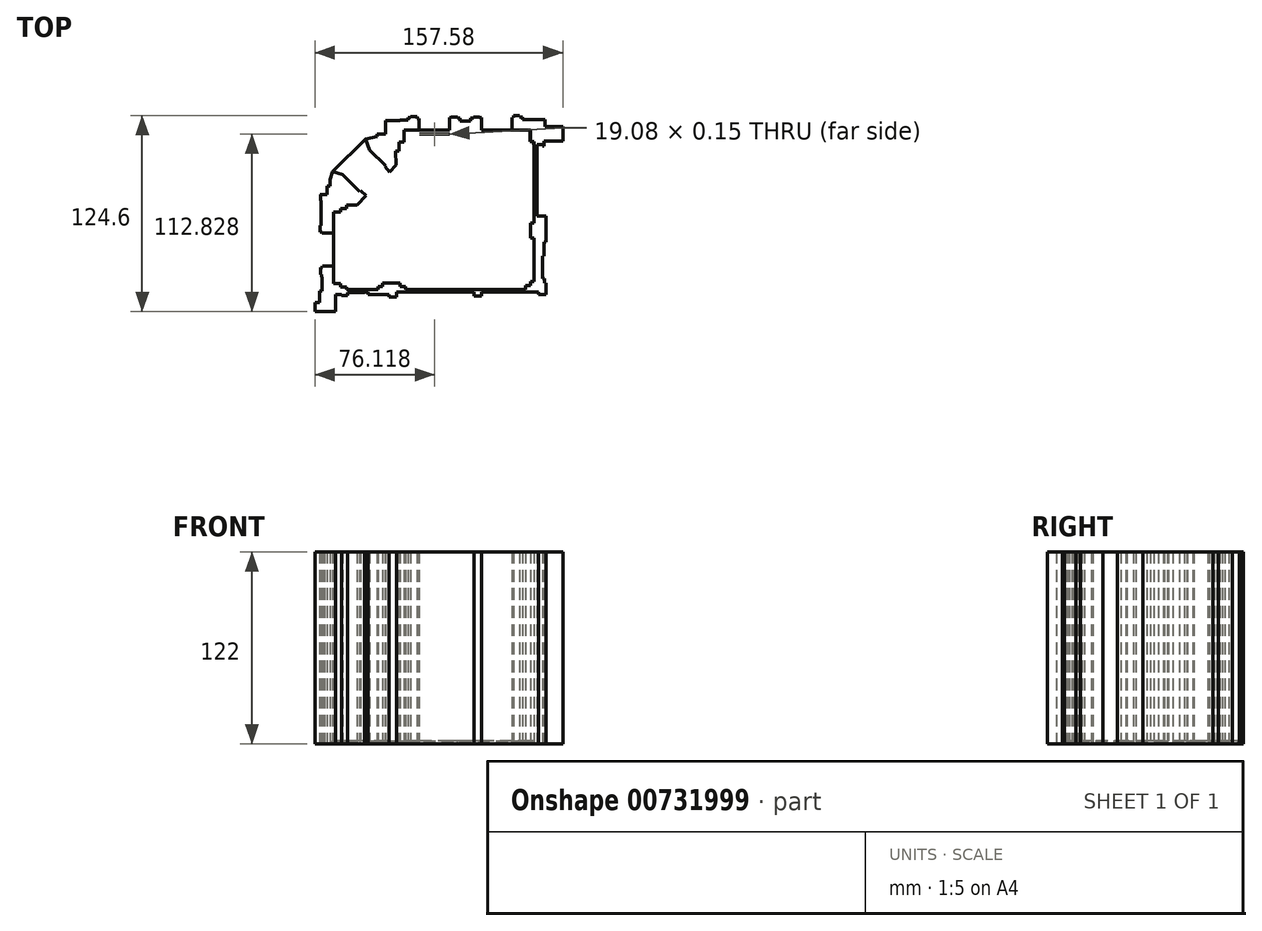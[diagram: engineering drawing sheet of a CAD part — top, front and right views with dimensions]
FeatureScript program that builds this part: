
annotation { "Feature Type Name" : "Feature", "Feature Type Description" : "" }
export const myFeature = defineFeature(function(context is Context, id is Id, definition is map)
    precondition{}
    {
        {
            var Q0;
            Q0=qCreatedBy(makeId("Top.planeOp"),FACE);
            var sketch = newSketch(context, id + "F0", { "sketchPlane" : qUnion([Q0])});
            skLineSegment(sketch, "E0", {"start": v(100, 30.78) * mm, "end": v(19.62, 30.78) * mm});
            skLineSegment(sketch, "E1", {"start": v(14.37, 17.38) * mm, "end": v(14.67, 8.47) * mm});
            skLineSegment(sketch, "E2", {"start": v(10.68, 4.23) * mm, "end": v(7.6, 7.76) * mm});
            skLineSegment(sketch, "E3", {"start": v(-10.22, -16.86) * mm, "end": v(-16.88, -16.86) * mm});
            skLineSegment(sketch, "E4", {"start": v(-16.88, -16.86) * mm, "end": v(-16.88, -19.03) * mm});
            skLineSegment(sketch, "E5", {"start": v(-16.88, -19.03) * mm, "end": v(-20.5, -19.03) * mm});
            skLineSegment(sketch, "E6", {"start": v(-20.5, -19.03) * mm, "end": v(-20.5, -21.2) * mm});
            skLineSegment(sketch, "E7", {"start": v(-20.5, -21.2) * mm, "end": v(-24.94, -21.2) * mm});
            skLineSegment(sketch, "E8", {"start": v(-24.94, -21.2) * mm, "end": v(-24.94, -66.6) * mm});
            skLineSegment(sketch, "E9", {"start": v(-24.94, -66.6) * mm, "end": v(-20.5, -66.6) * mm});
            skLineSegment(sketch, "E10", {"start": v(-20.5, -66.6) * mm, "end": v(-20.5, -68.85) * mm});
            skLineSegment(sketch, "E11", {"start": v(-20.5, -68.85) * mm, "end": v(-16.88, -68.85) * mm});
            skLineSegment(sketch, "E12", {"start": v(-16.88, -68.85) * mm, "end": v(-16.88, -70.47) * mm});
            skLineSegment(sketch, "E13", {"start": v(-16.88, -70.47) * mm, "end": v(3.12, -70.47) * mm});
            skLineSegment(sketch, "E14", {"start": v(3.12, -70.47) * mm, "end": v(3.12, -68.58) * mm});
            skLineSegment(sketch, "E15", {"start": v(3.12, -68.58) * mm, "end": v(6.2, -68.58) * mm});
            skLineSegment(sketch, "E16", {"start": v(6.2, -68.58) * mm, "end": v(6.2, -66.38) * mm});
            skLineSegment(sketch, "E17", {"start": v(6.2, -66.38) * mm, "end": v(17.27, -66.38) * mm});
            skLineSegment(sketch, "E18", {"start": v(17.27, -66.38) * mm, "end": v(17.27, -68.45) * mm});
            skLineSegment(sketch, "E19", {"start": v(17.27, -68.45) * mm, "end": v(20.68, -68.45) * mm});
            skLineSegment(sketch, "E20", {"start": v(20.68, -68.45) * mm, "end": v(20.68, -70.43) * mm});
            skLineSegment(sketch, "E21", {"start": v(20.68, -70.43) * mm, "end": v(96.86, -70.43) * mm});
            skLineSegment(sketch, "E22", {"start": v(96.86, -70.43) * mm, "end": v(96.86, -67.86) * mm});
            skLineSegment(sketch, "E23", {"start": v(96.86, -67.86) * mm, "end": v(100.14, -67.86) * mm});
            skLineSegment(sketch, "E24", {"start": v(100.14, -67.86) * mm, "end": v(100.14, -65.47) * mm});
            skLineSegment(sketch, "E25", {"start": v(100.14, -65.47) * mm, "end": v(102.3, -65.47) * mm});
            skLineSegment(sketch, "E26", {"start": v(102.3, -65.47) * mm, "end": v(102.3, -37.74) * mm});
            skLineSegment(sketch, "E27", {"start": v(102.3, -37.74) * mm, "end": v(100, -37.74) * mm});
            skLineSegment(sketch, "E28", {"start": v(100, -37.74) * mm, "end": v(100, -28.3) * mm});
            skLineSegment(sketch, "E29", {"start": v(100, -28.3) * mm, "end": v(102.15, -28.3) * mm});
            skLineSegment(sketch, "E30", {"start": v(102.15, -28.3) * mm, "end": v(102.15, 23.5) * mm});
            skLineSegment(sketch, "E31", {"start": v(102.15, 23.5) * mm, "end": v(100, 23.5) * mm});
            skLineSegment(sketch, "E32", {"start": v(100, 23.5) * mm, "end": v(100, 30.78) * mm});
            skLineSegment(sketch, "E33", {"start": v(102.15, -23.98) * mm, "end": v(109.78, -23.98) * mm});
            skLineSegment(sketch, "E34", {"start": v(109.78, -23.98) * mm, "end": v(109.78, -40.2) * mm});
            skLineSegment(sketch, "E35", {"start": v(109.78, -40.2) * mm, "end": v(108.53, -40.2) * mm});
            skLineSegment(sketch, "E36", {"start": v(108.53, -40.2) * mm, "end": v(108.53, -49.32) * mm});
            skLineSegment(sketch, "E37", {"start": v(108.53, -49.32) * mm, "end": v(107.6, -49.32) * mm});
            skLineSegment(sketch, "E38", {"start": v(107.6, -49.32) * mm, "end": v(107.6, -63.66) * mm});
            skLineSegment(sketch, "E39", {"start": v(107.6, -63.66) * mm, "end": v(108.9, -63.66) * mm});
            skLineSegment(sketch, "E40", {"start": v(108.9, -63.66) * mm, "end": v(108.9, -66.41) * mm});
            skLineSegment(sketch, "E41", {"start": v(108.9, -66.41) * mm, "end": v(109.78, -66.41) * mm});
            skLineSegment(sketch, "E42", {"start": v(109.78, -66.41) * mm, "end": v(109.78, -73.81) * mm});
            skLineSegment(sketch, "E43", {"start": v(109.78, -73.81) * mm, "end": v(105, -73.81) * mm});
            skLineSegment(sketch, "E44", {"start": v(105, -73.81) * mm, "end": v(105, -72.02) * mm});
            skLineSegment(sketch, "E45", {"start": v(105, -72.02) * mm, "end": v(68.84, -72.02) * mm});
            skLineSegment(sketch, "E46", {"start": v(68.84, -72.02) * mm, "end": v(68.84, -74.47) * mm});
            skLineSegment(sketch, "E47", {"start": v(68.84, -74.47) * mm, "end": v(64.15, -74.47) * mm});
            skLineSegment(sketch, "E48", {"start": v(64.15, -74.47) * mm, "end": v(64.15, -72.02) * mm});
            skLineSegment(sketch, "E49", {"start": v(64.15, -72.02) * mm, "end": v(15, -72.02) * mm});
            skLineSegment(sketch, "E50", {"start": v(15, -72.02) * mm, "end": v(15, -75.12) * mm});
            skLineSegment(sketch, "E51", {"start": v(15, -75.12) * mm, "end": v(10.3, -75.12) * mm});
            skLineSegment(sketch, "E52", {"start": v(10.3, -75.12) * mm, "end": v(10.3, -73.52) * mm});
            skLineSegment(sketch, "E53", {"start": v(10.3, -73.52) * mm, "end": v(-3.14, -73.52) * mm});
            skLineSegment(sketch, "E54", {"start": v(-3.14, -73.52) * mm, "end": v(-3.14, -72.02) * mm});
            skLineSegment(sketch, "E55", {"start": v(-3.14, -72.02) * mm, "end": v(-5.41, -72.02) * mm});
            skLineSegment(sketch, "E56", {"start": v(-16.3, -72.35) * mm, "end": v(-16.3, -74.28) * mm});
            skLineSegment(sketch, "E57", {"start": v(-16.3, -74.28) * mm, "end": v(-19.89, -74.28) * mm});
            skLineSegment(sketch, "E58", {"start": v(-19.89, -74.28) * mm, "end": v(-19.89, -73.55) * mm});
            skLineSegment(sketch, "E59", {"start": v(-19.89, -73.55) * mm, "end": v(-23.83, -73.55) * mm});
            skLineSegment(sketch, "E60", {"start": v(-23.83, -73.55) * mm, "end": v(-23.83, -84.62) * mm});
            skLineSegment(sketch, "E61", {"start": v(-23.83, -84.62) * mm, "end": v(-36.93, -84.62) * mm});
            skLineSegment(sketch, "E62", {"start": v(-36.93, -84.62) * mm, "end": v(-36.93, -78.83) * mm});
            skLineSegment(sketch, "E63", {"start": v(-36.93, -78.83) * mm, "end": v(-33.87, -78.83) * mm});
            skLineSegment(sketch, "E64", {"start": v(-33.87, -78.83) * mm, "end": v(-33.87, -71.33) * mm});
            skLineSegment(sketch, "E65", {"start": v(-33.87, -71.33) * mm, "end": v(-32.2, -71.33) * mm});
            skLineSegment(sketch, "E66", {"start": v(-32.2, -71.33) * mm, "end": v(-32.2, -62.56) * mm});
            skLineSegment(sketch, "E67", {"start": v(-32.2, -62.56) * mm, "end": v(-32.7, -62.56) * mm});
            skLineSegment(sketch, "E68", {"start": v(-32.7, -62.56) * mm, "end": v(-32.7, -60.9) * mm});
            skLineSegment(sketch, "E69", {"start": v(-32.7, -60.9) * mm, "end": v(-33.3, -60.9) * mm});
            skLineSegment(sketch, "E70", {"start": v(-33.3, -60.9) * mm, "end": v(-33.3, -56.5) * mm});
            skLineSegment(sketch, "E71", {"start": v(-33.3, -56.5) * mm, "end": v(-32.1, -56.5) * mm});
            skLineSegment(sketch, "E72", {"start": v(-32.1, -56.5) * mm, "end": v(-32.1, -55.62) * mm});
            skLineSegment(sketch, "E73", {"start": v(-32.1, -55.62) * mm, "end": v(-24.94, -55.62) * mm});
            skLineSegment(sketch, "E74.top", {"start": v(-16.3, -72.35) * mm, "end": v(-5.41, -72.35) * mm});
            skLineSegment(sketch, "E74.right", {"start": v(-5.41, -72.02) * mm, "end": v(-5.41, -72.35) * mm});
            skLineSegment(sketch, "E75", {"start": v(104.08, -23.98) * mm, "end": v(104.08, 21.47) * mm});
            skLineSegment(sketch, "E76.bottom", {"start": v(88.6, 28.28) * mm, "end": v(68.96, 28.28) * mm});
            skLineSegment(sketch, "E76.top", {"start": v(88.6, 17.82) * mm, "end": v(68.96, 17.82) * mm});
            skLineSegment(sketch, "E76.left", {"start": v(88.6, 28.28) * mm, "end": v(88.6, 17.82) * mm});
            skLineSegment(sketch, "E76.right", {"start": v(68.96, 28.28) * mm, "end": v(68.96, 17.82) * mm});
            skLineSegment(sketch, "E77.bottom", {"start": v(48.73, 28.28) * mm, "end": v(29.65, 28.28) * mm});
            skLineSegment(sketch, "E77.top", {"start": v(48.73, 17.82) * mm, "end": v(29.65, 17.82) * mm});
            skLineSegment(sketch, "E77.left", {"start": v(48.73, 28.28) * mm, "end": v(48.73, 17.82) * mm});
            skLineSegment(sketch, "E77.right", {"start": v(29.65, 28.28) * mm, "end": v(29.65, 17.82) * mm});
            skLineSegment(sketch, "E78", {"start": v(14.37, 17.38) * mm, "end": v(16.66, 17.38) * mm});
            skLineSegment(sketch, "E79", {"start": v(16.66, 17.38) * mm, "end": v(16.66, 23.03) * mm});
            skLineSegment(sketch, "E80", {"start": v(16.66, 23.03) * mm, "end": v(19.9, 23.03) * mm});
            skLineSegment(sketch, "E81", {"start": v(19.9, 23.03) * mm, "end": v(19.9, 30.78) * mm});
            skLineSegment(sketch, "E82", {"start": v(19.9, 30.78) * mm, "end": v(29.26, 30.78) * mm});
            skLineSegment(sketch, "E83", {"start": v(29.26, 30.78) * mm, "end": v(29.26, 38.23) * mm});
            skLineSegment(sketch, "E84", {"start": v(29.26, 38.23) * mm, "end": v(28.12, 38.23) * mm});
            skLineSegment(sketch, "E85", {"start": v(28.12, 38.23) * mm, "end": v(28.12, 39.27) * mm});
            skLineSegment(sketch, "E86", {"start": v(28.12, 39.27) * mm, "end": v(23.9, 39.27) * mm});
            skLineSegment(sketch, "E87", {"start": v(23.9, 39.27) * mm, "end": v(23.9, 38.64) * mm});
            skLineSegment(sketch, "E88", {"start": v(23.9, 38.64) * mm, "end": v(22.3, 38.64) * mm});
            skLineSegment(sketch, "E89", {"start": v(22.3, 38.64) * mm, "end": v(22.3, 37.04) * mm});
            skLineSegment(sketch, "E90", {"start": v(22.3, 37.04) * mm, "end": v(17.2, 37.04) * mm});
            skLineSegment(sketch, "E91", {"start": v(17.2, 37.04) * mm, "end": v(17.2, 36.7) * mm});
            skLineSegment(sketch, "E92", {"start": v(17.2, 36.7) * mm, "end": v(7.86, 36.7) * mm});
            skLineSegment(sketch, "E93", {"start": v(7.86, 36.7) * mm, "end": v(8.12, 28.3) * mm});
            skLineSegment(sketch, "E94", {"start": v(8.12, 28.3) * mm, "end": v(2.65, 28.3) * mm});
            skLineSegment(sketch, "E95", {"start": v(2.65, 28.3) * mm, "end": v(2.65, 26.75) * mm});
            skLineSegment(sketch, "E96", {"start": v(2.65, 26.75) * mm, "end": v(-4.82, 25.12) * mm});
            skLineSegment(sketch, "E97", {"start": v(-4.82, 25.12) * mm, "end": v(-2.29, 18.24) * mm});
            skLineSegment(sketch, "E98", {"start": v(8.12, 8.35) * mm, "end": v(-2.29, 18.24) * mm});
            skLineSegment(sketch, "E99", {"start": v(8.12, 8.35) * mm, "end": v(7.6, 7.76) * mm});
            skLineSegment(sketch, "E100", {"start": v(-4.42, -10.92) * mm, "end": v(-10.22, -16.86) * mm});
            skLineSegment(sketch, "E101", {"start": v(-24.94, -34.61) * mm, "end": v(-32.4, -34.61) * mm});
            skLineSegment(sketch, "E102", {"start": v(-33.67, -33.94) * mm, "end": v(-33.67, -29.77) * mm});
            skLineSegment(sketch, "E103", {"start": v(-33.67, -29.77) * mm, "end": v(-33.03, -29.77) * mm});
            skLineSegment(sketch, "E104", {"start": v(-33.03, -29.77) * mm, "end": v(-33.03, -13.85) * mm});
            skLineSegment(sketch, "E105", {"start": v(-33.03, -13.85) * mm, "end": v(-33.37, -13.85) * mm});
            skLineSegment(sketch, "E106", {"start": v(-33.37, -13.85) * mm, "end": v(-33.37, -10.27) * mm});
            skLineSegment(sketch, "E107", {"start": v(-33.67, -10.27) * mm, "end": v(-33.37, -10.27) * mm});
            skLineSegment(sketch, "E108", {"start": v(-33.67, -10.27) * mm, "end": v(-33.67, -10.09) * mm});
            skLineSegment(sketch, "E109", {"start": v(-33.67, -10.09) * mm, "end": v(-30.72, -10.09) * mm});
            skLineSegment(sketch, "E110", {"start": v(-29.22, -10.27) * mm, "end": v(-29.22, -4.8) * mm});
            skLineSegment(sketch, "E111", {"start": v(-29.22, -4.8) * mm, "end": v(-27.15, -4.8) * mm});
            skLineSegment(sketch, "E112", {"start": v(-27.15, -4.8) * mm, "end": v(-27.15, -0.77) * mm});
            skLineSegment(sketch, "E113", {"start": v(-27.15, -0.77) * mm, "end": v(-25.68, 4.32) * mm});
            skLineSegment(sketch, "E114", {"start": v(-25.68, 4.32) * mm, "end": v(-19.3, 2.48) * mm});
            skLineSegment(sketch, "E115", {"start": v(-19.3, 2.48) * mm, "end": v(-8.62, -8.4) * mm});
            skLineSegment(sketch, "E116", {"start": v(-8.62, -8.4) * mm, "end": v(-7.74, -7.67) * mm});
            skLineSegment(sketch, "E117", {"start": v(-30.72, -10.09) * mm, "end": v(-30.72, -10.27) * mm});
            skLineSegment(sketch, "E118", {"start": v(-30.72, -10.27) * mm, "end": v(-29.22, -10.27) * mm});
            skLineSegment(sketch, "E119", {"start": v(-4.42, -10.92) * mm, "end": v(-7.74, -7.67) * mm});
            skLineSegment(sketch, "E120", {"start": v(-32.4, -34.61) * mm, "end": v(-32.4, -33.94) * mm});
            skLineSegment(sketch, "E121", {"start": v(-32.4, -33.94) * mm, "end": v(-33.67, -33.94) * mm});
            skPoint(sketch, "E122.orphan", {"position": v(-33.67, -34.61) * mm});
            skLineSegment(sketch, "E123", {"start": v(48.76, 30.78) * mm, "end": v(69.02, 30.78) * mm});
            skLineSegment(sketch, "E124", {"start": v(69.02, 30.78) * mm, "end": v(69.02, 38.67) * mm});
            skLineSegment(sketch, "E125", {"start": v(69.02, 38.67) * mm, "end": v(67.73, 38.67) * mm});
            skLineSegment(sketch, "E126", {"start": v(67.73, 38.67) * mm, "end": v(67.73, 39) * mm});
            skLineSegment(sketch, "E127", {"start": v(67.73, 39) * mm, "end": v(63.74, 39) * mm});
            skLineSegment(sketch, "E128", {"start": v(63.74, 39) * mm, "end": v(63.74, 38.36) * mm});
            skLineSegment(sketch, "E129", {"start": v(63.74, 38.36) * mm, "end": v(62.08, 38.36) * mm});
            skLineSegment(sketch, "E130", {"start": v(62.08, 38.36) * mm, "end": v(62.08, 36.47) * mm});
            skLineSegment(sketch, "E131", {"start": v(62.08, 36.47) * mm, "end": v(55.28, 36.47) * mm});
            skLineSegment(sketch, "E132", {"start": v(55.28, 36.47) * mm, "end": v(55.28, 38.36) * mm});
            skLineSegment(sketch, "E133", {"start": v(55.28, 38.36) * mm, "end": v(53.72, 38.36) * mm});
            skLineSegment(sketch, "E134", {"start": v(53.72, 38.36) * mm, "end": v(53.72, 39) * mm});
            skLineSegment(sketch, "E135", {"start": v(53.72, 39) * mm, "end": v(49.68, 39) * mm});
            skLineSegment(sketch, "E136", {"start": v(49.68, 39) * mm, "end": v(49.68, 38.67) * mm});
            skLineSegment(sketch, "E137", {"start": v(49.68, 38.67) * mm, "end": v(48.76, 38.67) * mm});
            skLineSegment(sketch, "E138", {"start": v(48.76, 38.67) * mm, "end": v(48.76, 30.78) * mm});
            skLineSegment(sketch, "E139", {"start": v(99.67, 30.78) * mm, "end": v(99.67, 23.5) * mm});
            skLineSegment(sketch, "E140", {"start": v(99.67, 23.5) * mm, "end": v(102.12, 23.5) * mm});
            skLineSegment(sketch, "E141", {"start": v(102.12, 23.5) * mm, "end": v(102.12, 21.47) * mm});
            skLineSegment(sketch, "E142", {"start": v(102.12, 21.47) * mm, "end": v(107.62, 21.47) * mm});
            skLineSegment(sketch, "E143", {"start": v(107.62, 21.47) * mm, "end": v(107.62, 20.5) * mm});
            skLineSegment(sketch, "E144", {"start": v(107.62, 20.5) * mm, "end": v(108.74, 20.5) * mm});
            skLineSegment(sketch, "E145", {"start": v(108.74, 20.5) * mm, "end": v(108.74, 23.95) * mm});
            skLineSegment(sketch, "E146", {"start": v(108.74, 23.95) * mm, "end": v(120.65, 23.95) * mm});
            skLineSegment(sketch, "E147", {"start": v(120.65, 23.95) * mm, "end": v(120.65, 32.97) * mm});
            skLineSegment(sketch, "E148", {"start": v(120.65, 32.97) * mm, "end": v(109.3, 32.97) * mm});
            skLineSegment(sketch, "E149", {"start": v(109.3, 32.97) * mm, "end": v(109.3, 37.43) * mm});
            skLineSegment(sketch, "E150", {"start": v(109.3, 37.43) * mm, "end": v(94.85, 37.43) * mm});
            skLineSegment(sketch, "E151", {"start": v(94.85, 37.43) * mm, "end": v(94.85, 39.05) * mm});
            skLineSegment(sketch, "E152", {"start": v(94.85, 39.05) * mm, "end": v(93.23, 39.05) * mm});
            skLineSegment(sketch, "E153", {"start": v(93.23, 39.05) * mm, "end": v(93.23, 39.98) * mm});
            skLineSegment(sketch, "E154", {"start": v(93.23, 39.98) * mm, "end": v(89.15, 39.98) * mm});
            skLineSegment(sketch, "E155", {"start": v(89.15, 39.98) * mm, "end": v(89.15, 38.67) * mm});
            skLineSegment(sketch, "E156", {"start": v(89.15, 38.67) * mm, "end": v(88.27, 38.67) * mm});
            skLineSegment(sketch, "E157", {"start": v(88.27, 38.67) * mm, "end": v(88.27, 30.78) * mm});
            skLineSegment(sketch, "E158", {"start": v(88.27, 30.78) * mm, "end": v(99.67, 30.78) * mm});
            skLineSegment(sketch, "E159.bottom", {"start": v(48.76, 28.13) * mm, "end": v(29.26, 28.13) * mm});
            skLineSegment(sketch, "E159.left", {"start": v(48.76, 28.13) * mm, "end": v(48.76, 18.13) * mm});
            skLineSegment(sketch, "E159.right", {"start": v(29.26, 28.13) * mm, "end": v(29.26, 18.13) * mm});
            skLineSegment(sketch, "E160.bottom", {"start": v(-22.44, -34.61) * mm, "end": v(-12.44, -34.61) * mm});
            skLineSegment(sketch, "E160.top", {"start": v(-22.44, -55.62) * mm, "end": v(-12.44, -55.62) * mm});
            skLineSegment(sketch, "E160.left", {"start": v(-22.44, -34.61) * mm, "end": v(-22.44, -55.62) * mm});
            skLineSegment(sketch, "E160.right", {"start": v(-12.44, -34.61) * mm, "end": v(-12.44, -55.62) * mm});
            skLineSegment(sketch, "E161", {"start": v(10.68, 4.23) * mm, "end": v(14.67, 8.47) * mm});
            skLineSegment(sketch, "E162", {"start": v(10.68, 4.23) * mm, "end": v(-4.42, -10.92) * mm});
            skFitSpline(sketch, "E163", {"points": [v(102.15, 8.94) * mm, v(78.29, 3.93) * mm, v(66.58, -13.62) * mm, v(53.72, -35.8) * mm, v(24.2, -40.24) * mm, v(1.71, -50.69) * mm, v(-5.41, -70.47) * mm], "startDerivative": vector(-103.23, 11.75) * mm, "endDerivative": vector(-2.21, -218.2) * mm});
            skLineSegment(sketch, "E164", {"start": v(102.15, -15.64) * mm, "end": v(55.24, -70.43) * mm, "construction": true});
            skArc(sketch, "E165", {"start": v(100, -28.3) * mm, "mid": v(70.38, -40.66) * mm, "end": v(58.36, -70.43) * mm});
            skLineSegment(sketch, "E166", {"start": v(100, -28.3) * mm, "end": v(75.52, -28.3) * mm, "construction": true});
            skLineSegment(sketch, "E167", {"start": v(-4.82, 25.12) * mm, "end": v(-25.68, 4.32) * mm});
            skSolve(sketch);
        }
        {
            var Q0;
            {var subQ6=sQuery(id+"F0.wireOp",EDGE,"E9");Q0=makeQuery(id+"F0.imprint","IMPRINT",FACE,{"disambiguationData":[TD([[makeQuery(id+"F0.imprint","IMPRINT",EDGE,{"derivedFrom":subQ6}),-1.0]])]});}
            var Q1;
            {var subQ7=sQuery(id+"F0.wireOp",EDGE,"E31");Q1=makeQuery(id+"F0.imprint","IMPRINT",FACE,{"disambiguationData":[TD([[makeQuery(id+"F0.imprint","IMPRINT",EDGE,{"derivedFrom":subQ7}),-1.0]])]});}
            var Q2;
            {var subQ5=sQuery(id+"F0.wireOp",EDGE,"E75");Q2=makeQuery(id+"F0.imprint","IMPRINT",FACE,{"disambiguationData":[TD([[makeQuery(id+"F0.imprint","IMPRINT",EDGE,{"derivedFrom":subQ5}),1.0]])]});}
            extrude(context, id + "F1", {"entities" : qUnion([Q0, Q1, Q2]), "depth" : 120 * mm, "offsetDistance" : 25 * mm});
        }
        {
            var Q0;
            Q0=makeQuery(id+"F0.imprint","IMPRINT",FACE,{"disambiguationData":[TD([[makeQuery(id+"F0.imprint","IMPRINT",EDGE,{"derivedFrom":sQuery(id+"F0.wireOp",EDGE,"E123")}),1.0]])]});
            var Q1;
            Q1=makeQuery(id+"F0.imprint","IMPRINT",FACE,{"disambiguationData":[TD([[makeQuery(id+"F0.imprint","IMPRINT",EDGE,{"derivedFrom":sQuery(id+"F0.wireOp",EDGE,"E1")}),-1.0]])]});
            var Q2;
            Q2=makeQuery(id+"F0.imprint","IMPRINT",FACE,{"disambiguationData":[TD([[makeQuery(id+"F0.imprint","IMPRINT",EDGE,{"derivedFrom":sQuery(id+"F0.wireOp",EDGE,"E3")}),-1.0]])]});
            extrude(context, id + "F2", {"entities" : qUnion([Q0, Q1, Q2]), "depth" : 120 * mm, "offsetDistance" : 25 * mm});
        }
        {
            var Q0;
            Q0 = qSketchRegion(id + "F0", true);
            var Q1;
            Q1=makeQuery(id+"F0.imprint","IMPRINT",FACE,{"disambiguationData":[TD([[makeQuery(id+"F0.imprint","IMPRINT",EDGE,{"derivedFrom":sQuery(id+"F0.wireOp",EDGE,"E160.bottom")}),-1.0]])]});
            var Q2;
            {var subQ5=sQuery(id+"F0.wireOp",EDGE,"E14");Q2=makeQuery(id+"F0.imprint","IMPRINT",FACE,{"disambiguationData":[TD([[makeQuery(id+"F0.imprint","IMPRINT",EDGE,{"derivedFrom":subQ5}),1.0]])]});}
            var Q3;
            {var subQ0=sQuery(id+"F0.wireOp",EDGE,"E22");Q3=makeQuery(id+"F0.imprint","IMPRINT",FACE,{"disambiguationData":[TD([[makeQuery(id+"F0.imprint","IMPRINT",EDGE,{"derivedFrom":subQ0}),1.0]])]});}
            var Q4;
            Q4=makeQuery(id+"F0.imprint","IMPRINT",FACE,{"disambiguationData":[TD([[makeQuery(id+"F0.imprint","IMPRINT",EDGE,{"derivedFrom":sQuery(id+"F0.wireOp",EDGE,"E76.bottom")}),1.0]])]});
            var Q5;
            {var subQ0=sQuery(id+"F0.wireOp",EDGE,"E77.top");Q5=makeQuery(id+"F0.imprint","IMPRINT",FACE,{"disambiguationData":[TD([[makeQuery(id+"F0.imprint","IMPRINT",EDGE,{"derivedFrom":subQ0}),-1.0]])]});}
            extrude(context, id + "F3", {"entities" : qUnion([Q0, Q1, Q2, Q3, Q4, Q5]), "operationType" : NewBodyOperationType.ADD, "oppositeDirection" : true, "depth" : 2 * mm, "offsetDistance" : 25 * mm});
        }
    });
